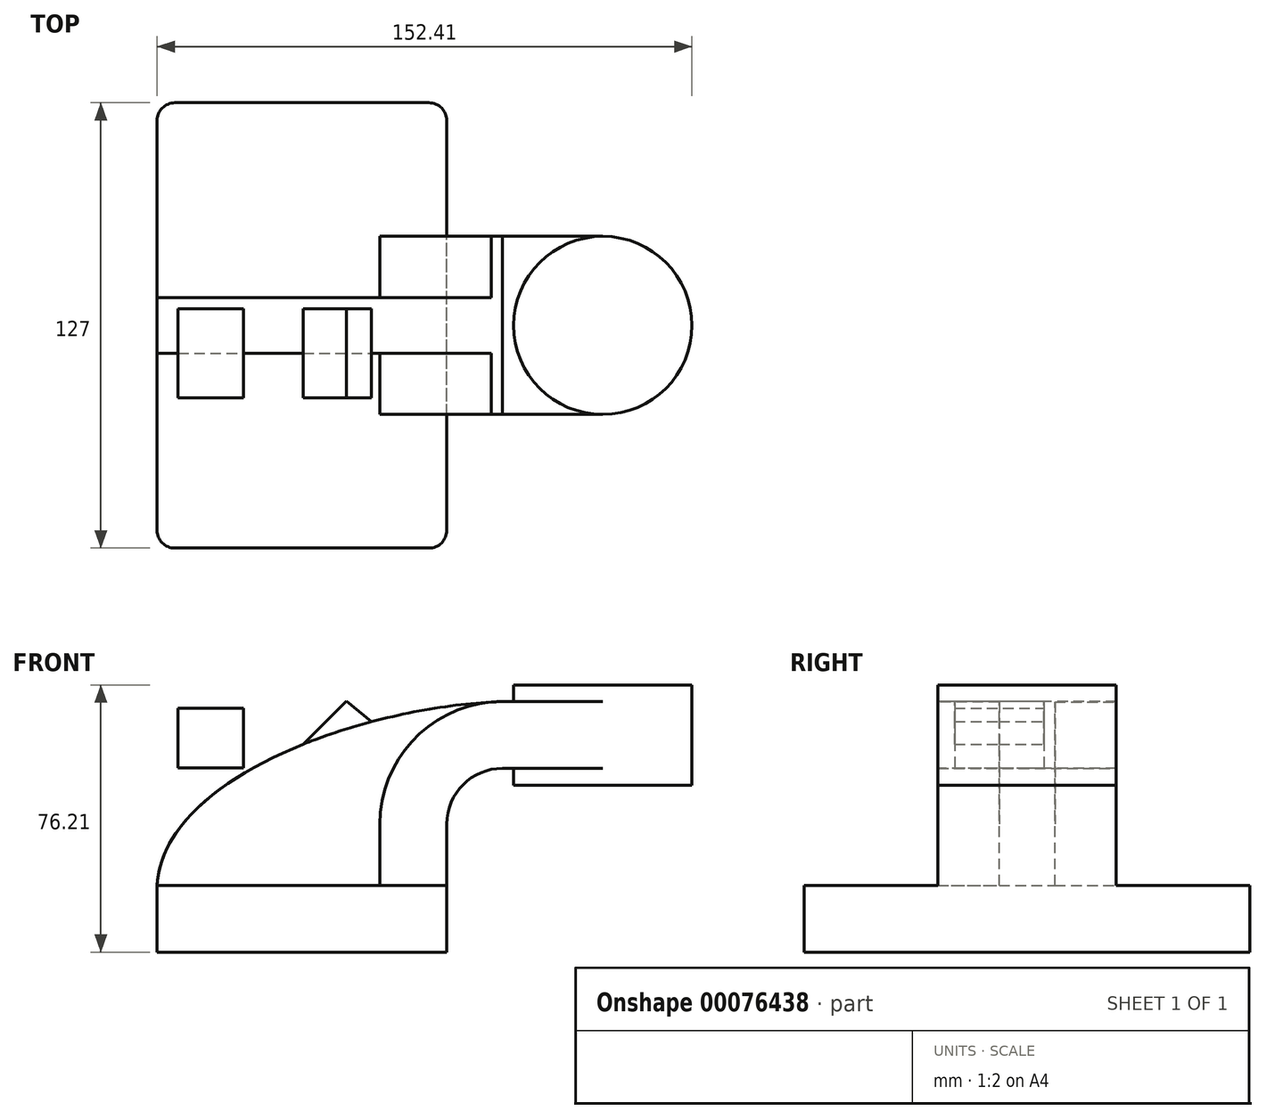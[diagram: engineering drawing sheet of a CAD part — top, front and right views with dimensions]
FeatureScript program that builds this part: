
annotation { "Feature Type Name" : "Feature", "Feature Type Description" : "" }
export const myFeature = defineFeature(function(context is Context, id is Id, definition is map)
    precondition{}
    {
        {
            var Q0;
            Q0=qCreatedBy(makeId("Front.planeOp"),FACE);
            var sketch = newSketch(context, id + "F0", { "sketchPlane" : qUnion([Q0])});
            skLineSegment(sketch, "E0.rect.bottom", {"start": v(-41.28, 9.52) * mm, "end": v(41.28, 9.52) * mm});
            skLineSegment(sketch, "E0.rect.top", {"start": v(-41.28, -9.52) * mm, "end": v(41.28, -9.52) * mm});
            skLineSegment(sketch, "E0.rect.left", {"start": v(-41.28, 9.52) * mm, "end": v(-41.28, -9.52) * mm});
            skLineSegment(sketch, "E0.rect.right", {"start": v(41.28, 9.52) * mm, "end": v(41.28, -9.52) * mm});
            skPoint(sketch, "E0.rect.middle", {"position": v(0, 0) * mm});
            skLineSegment(sketch, "E1", {"start": v(41.28, 9.52) * mm, "end": v(41.28, 27) * mm});
            skArc(sketch, "E2", {"start": v(41.28, 27) * mm, "mid": v(45.92, 38.23) * mm, "end": v(57.15, 42.88) * mm});
            skLineSegment(sketch, "E3", {"start": v(57.15, 42.88) * mm, "end": v(85.72, 42.88) * mm});
            skLineSegment(sketch, "E4.rect.bottom", {"start": v(60.32, 38.1) * mm, "end": v(111.12, 38.1) * mm});
            skLineSegment(sketch, "E4.rect.top", {"start": v(60.32, 66.68) * mm, "end": v(111.12, 66.68) * mm});
            skLineSegment(sketch, "E4.rect.left", {"start": v(60.32, 38.1) * mm, "end": v(60.32, 66.68) * mm});
            skLineSegment(sketch, "E4.rect.right", {"start": v(111.13, 38.1) * mm, "end": v(111.12, 66.68) * mm});
            skPoint(sketch, "E4.rect.middle", {"position": v(85.72, 52.39) * mm});
            skLineSegment(sketch, "E5.0", {"start": v(57.15, 61.93) * mm, "end": v(85.72, 61.93) * mm});
            skArc(sketch, "E5.1", {"start": v(22.23, 27) * mm, "mid": v(32.45, 51.7) * mm, "end": v(57.15, 61.93) * mm});
            skLineSegment(sketch, "E5.2", {"start": v(22.23, 9.52) * mm, "end": v(22.23, 27) * mm});
            skLineSegment(sketch, "E6", {"start": v(85.72, 38.1) * mm, "end": v(85.72, 66.68) * mm});
            skFitSpline(sketch, "E7", {"points": [v(-41.28, 9.53) * mm, v(57.15, 61.93) * mm], "startDerivative": vector(5.2, 92.34) * mm, "endDerivative": vector(120.92, 4.22) * mm});
            skSolve(sketch);
        }
        {
            var Q0;
            Q0=makeQuery(id+"F0.imprint","IMPRINT",FACE,{"disambiguationData":[TD([[makeQuery(id+"F0.imprint","IMPRINT",EDGE,{"derivedFrom":sQuery(id+"F0.wireOp",EDGE,"E0.rect.top")}),1.0]])]});
            extrude(context, id + "F1", {"entities" : qUnion([Q0]), "endBound" : BoundingType.SYMMETRIC, "depth" : 127 * mm});
        }
        {
            var Q0;
            {var subQ9=sQuery(id+"F0.wireOp",EDGE,"E1");Q0=makeQuery(id+"F0.imprint","IMPRINT",FACE,{"disambiguationData":[TD([[makeQuery(id+"F0.imprint","IMPRINT",EDGE,{"derivedFrom":subQ9}),1.0]])]});}
            var Q1;
            {var subQ0=sQuery(id+"F0.wireOp",EDGE,"E6");var subQ1=sQuery(id+"F0.wireOp",EDGE,"E3");var subQ2=makeQuery(id+"F0.imprint","INTERSECT",VERTEX,{"derivedFrom":[subQ1,subQ0]});Q1=makeQuery(id+"F0.imprint","IMPRINT",FACE,{"disambiguationData":[TD([[makeQuery(id+"F0.imprint","IMPRINT",EDGE,{"disambiguationData":[TD([[subQ2,1.0]])],"derivedFrom":subQ1}),1.0]])]});}
            extrude(context, id + "F2", {"entities" : qUnion([Q0, Q1]), "operationType" : NewBodyOperationType.ADD, "endBound" : BoundingType.SYMMETRIC, "depth" : 50.8 * mm});
        }
        {
            var Q0;
            {var subQ3=sQuery(id+"F0.wireOp",EDGE,"E5.2");Q0=makeQuery(id+"F0.imprint","IMPRINT",FACE,{"disambiguationData":[TD([[makeQuery(id+"F0.imprint","IMPRINT",EDGE,{"derivedFrom":subQ3}),1.0]])]});}
            extrude(context, id + "F3", {"entities" : qUnion([Q0]), "operationType" : NewBodyOperationType.ADD, "endBound" : BoundingType.SYMMETRIC, "depth" : 15.88 * mm});
        }
        {
            var Q0;
            {var subQ5=sQuery(id+"F0.wireOp",EDGE,"E4.rect.right");Q0=makeQuery(id+"F0.imprint","IMPRINT",FACE,{"disambiguationData":[TD([[makeQuery(id+"F0.imprint","IMPRINT",EDGE,{"derivedFrom":subQ5}),1.0]])]});}
            var Q1;
            Q1=sQuery(id+"F0.wireOp",EDGE,"E6");
            revolve(context, id + "F4", {"operationType" : NewBodyOperationType.ADD, "entities" : qUnion([Q0]), "axis" : qUnion([Q1]), "revolveType" : RevolveType.FULL});
        }
        {
            var Q0;
            Q0=makeQuery(id+"F1.opExtrude","CAP_EDGE",EDGE,{"disambiguationData":[OSD([sQuery(id+"F0.wireOp",EDGE,"E0.rect.right")])],"isStart":false});
            var Q1;
            Q1=makeQuery(id+"F1.opExtrude","CAP_EDGE",EDGE,{"disambiguationData":[OSD([sQuery(id+"F0.wireOp",EDGE,"E0.rect.left")])],"isStart":false});
            var Q2;
            Q2=makeQuery(id+"F1.opExtrude","CAP_EDGE",EDGE,{"disambiguationData":[OSD([sQuery(id+"F0.wireOp",EDGE,"E0.rect.right")])],"isStart":true});
            var Q3;
            Q3=makeQuery(id+"F1.opExtrude","CAP_EDGE",EDGE,{"disambiguationData":[OSD([sQuery(id+"F0.wireOp",EDGE,"E0.rect.left")])],"isStart":true});
            fillet(context, id + "F5", {"entities" : qUnion([Q0, Q1, Q2, Q3]), "radius" : 5.08 * mm, "tangentPropagation" : true, "allowEdgeOverflow" : false});
        }
        {
            var Q0;
            Q0=makeQuery(id+"F3.opExtrude","CAP_FACE",FACE,{"disambiguationData":[OSD([sQuery(id+"F0.wireOp",EDGE,"E0.rect.bottom"),sQuery(id+"F0.wireOp",EDGE,"E5.1"),sQuery(id+"F0.wireOp",EDGE,"E5.2"),sQuery(id+"F0.wireOp",EDGE,"E7")])],"isStart":false});
            var sketch = newSketch(context, id + "F6", { "sketchPlane" : qUnion([Q0])});
            skLineSegment(sketch, "E8", {"start": v(-22.74, 26.66) * mm, "end": v(55.3, 26.66) * mm});
            skLineSegment(sketch, "E9", {"start": v(55.3, 26.66) * mm, "end": v(12.7, 62.1) * mm});
            skLineSegment(sketch, "E10", {"start": v(12.7, 62.1) * mm, "end": v(-22.74, 26.66) * mm});
            skLineSegment(sketch, "E11.bottom", {"start": v(-35.3, 59.98) * mm, "end": v(-16.65, 59.98) * mm});
            skLineSegment(sketch, "E11.top", {"start": v(-35.3, 43.06) * mm, "end": v(-16.65, 43.06) * mm});
            skLineSegment(sketch, "E11.left", {"start": v(-35.3, 59.98) * mm, "end": v(-35.3, 43.06) * mm});
            skLineSegment(sketch, "E11.right", {"start": v(-16.65, 59.98) * mm, "end": v(-16.65, 43.06) * mm});
            skSolve(sketch);
        }
        {
            var Q0;
            Q0=makeQuery(id+"F6.imprint","IMPRINT",FACE,{"disambiguationData":[TD([[makeQuery(id+"F6.imprint","IMPRINT",EDGE,{"derivedFrom":sQuery(id+"F6.wireOp",EDGE,"E11.bottom")}),-1.0]])]});
            var Q1;
            {var subQ0=sQuery(id+"F6.wireOp",EDGE,"E10");var subQ1=sQuery(id+"F6.wireOp",EDGE,"E9");var subQ2=makeQuery(id+"F6.imprint","INTERSECT",VERTEX,{"derivedFrom":[subQ1,subQ0]});Q1=makeQuery(id+"F6.imprint","IMPRINT",FACE,{"disambiguationData":[TD([[makeQuery(id+"F6.imprint","IMPRINT",EDGE,{"disambiguationData":[TD([[subQ2,1.0]])],"derivedFrom":subQ1}),1.0]])]});}
            extrude(context, id + "F7", {"entities" : qUnion([Q0, Q1]), "operationType" : NewBodyOperationType.ADD, "endBound" : BoundingType.SYMMETRIC, "depth" : 25.4 * mm});
        }
    });
